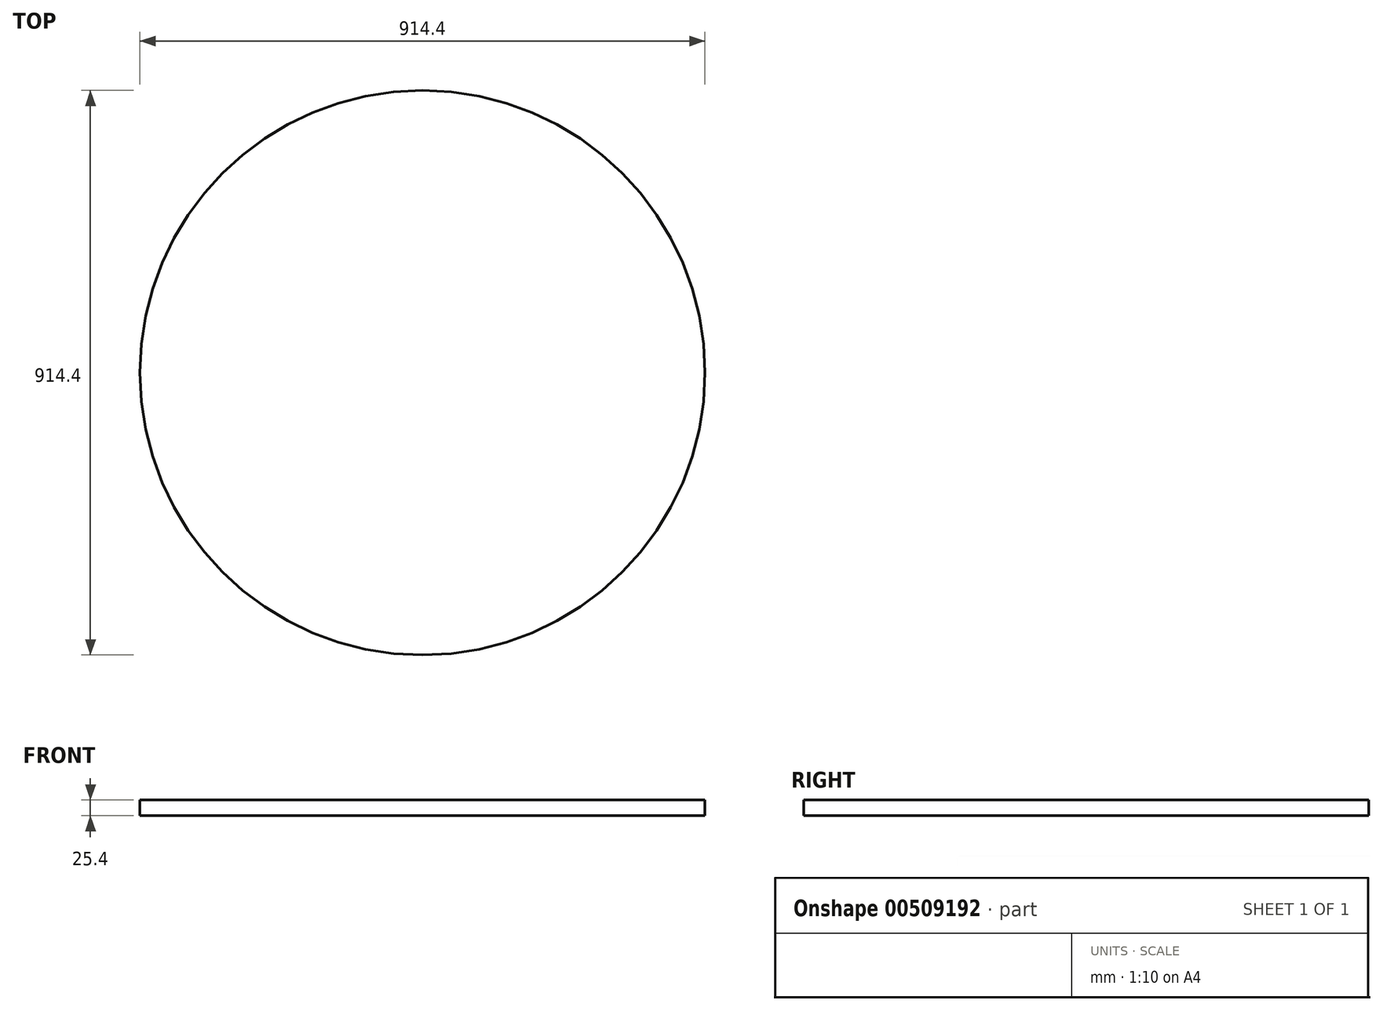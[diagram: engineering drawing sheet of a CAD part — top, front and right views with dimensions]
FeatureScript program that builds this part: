
annotation { "Feature Type Name" : "Feature", "Feature Type Description" : "" }
export const myFeature = defineFeature(function(context is Context, id is Id, definition is map)
    precondition{}
    {
        {
            var Q0;
            Q0=qCreatedBy(makeId("Top.planeOp"),FACE);
            var sketch = newSketch(context, id + "F0", { "sketchPlane" : qUnion([Q0])});
            skCircle(sketch, "E0", {"center": v(0, 0) * mm, "radius": 457.2 * mm});
            skSolve(sketch);
        }
        {
            var Q0;
            Q0=makeQuery(id+"F0.imprint","IMPRINT",FACE,{"disambiguationData":[TD([[makeQuery(id+"F0.imprint","IMPRINT",EDGE,{"derivedFrom":sQuery(id+"F0.wireOp",EDGE,"E0")}),1.0]])]});
            extrude(context, id + "F1", {"entities" : qUnion([Q0]), "endBound" : BoundingType.SYMMETRIC, "depth" : 25.4 * mm});
        }
    });
